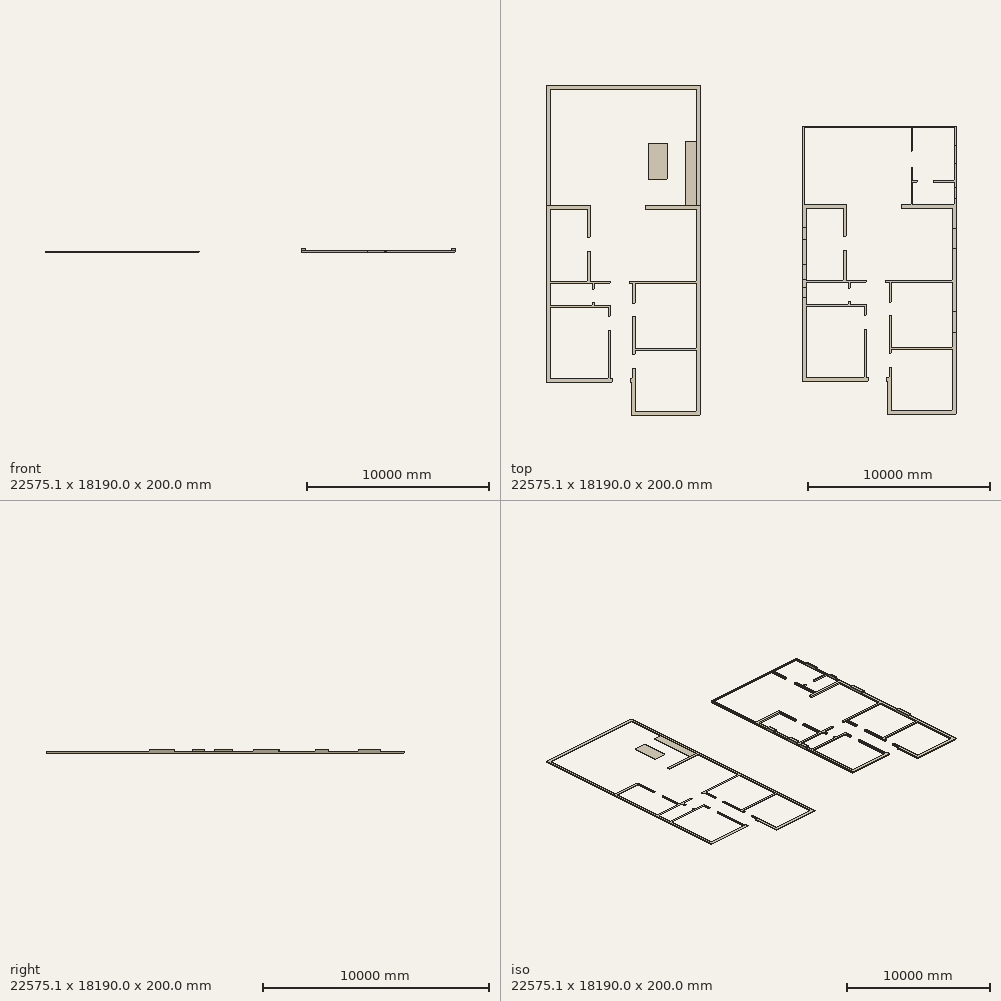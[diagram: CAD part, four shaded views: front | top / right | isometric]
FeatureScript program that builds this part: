
annotation { "Feature Type Name" : "Feature", "Feature Type Description" : "" }
export const myFeature = defineFeature(function(context is Context, id is Id, definition is map)
    precondition{}
    {
        {
            var Q0;
            Q0=qCreatedBy(makeId("Top.planeOp"),FACE);
            var sketch = newSketch(context, id + "F0", { "sketchPlane" : qUnion([Q0])});
            skLineSegment(sketch, "E0", {"start": v(-3410, -4400) * mm, "end": v(-3410, 5380) * mm});
            skLineSegment(sketch, "E1", {"start": v(-3410, 5380) * mm, "end": v(-1010, 5380) * mm});
            skLineSegment(sketch, "E2", {"start": v(5060, 5380) * mm, "end": v(5060, -6200) * mm});
            skLineSegment(sketch, "E3", {"start": v(5060, -6200) * mm, "end": v(1250, -6200) * mm});
            skLineSegment(sketch, "E4", {"start": v(1250, -6200) * mm, "end": v(1250, -4400) * mm});
            skLineSegment(sketch, "E5", {"start": v(240, -4400) * mm, "end": v(-3410, -4400) * mm});
            skLineSegment(sketch, "E6.bottom", {"start": v(1480, -5970) * mm, "end": v(4830, -5970) * mm});
            skLineSegment(sketch, "E6.left", {"start": v(1480, -5970) * mm, "end": v(1480, -3590) * mm});
            skLineSegment(sketch, "E6.right", {"start": v(4830, -5970) * mm, "end": v(4830, -2630) * mm});
            skLineSegment(sketch, "E7", {"start": v(1350, -2840) * mm, "end": v(1350, -730) * mm});
            skLineSegment(sketch, "E8", {"start": v(1350, -730) * mm, "end": v(1480, -730) * mm});
            skLineSegment(sketch, "E9", {"start": v(1480, -730) * mm, "end": v(1480, -2500) * mm});
            skLineSegment(sketch, "E10", {"start": v(1480, -2500) * mm, "end": v(4830, -2500) * mm});
            skLineSegment(sketch, "E11", {"start": v(4830, -2500) * mm, "end": v(4830, 1060) * mm});
            skLineSegment(sketch, "E12", {"start": v(4830, 1060) * mm, "end": v(1480, 1060) * mm});
            skLineSegment(sketch, "E13", {"start": v(1480, 0) * mm, "end": v(1350, 0) * mm});
            skLineSegment(sketch, "E14.bottom", {"start": v(-3180, -4170) * mm, "end": v(0, -4170) * mm});
            skLineSegment(sketch, "E14.top", {"start": v(-3180, -240) * mm, "end": v(0, -240) * mm});
            skLineSegment(sketch, "E14.left", {"start": v(-3180, -4170) * mm, "end": v(-3180, -240) * mm});
            skLineSegment(sketch, "E14.right", {"start": v(0, -4170) * mm, "end": v(0, -1500) * mm});
            skLineSegment(sketch, "E15.bottom", {"start": v(-3180, 1060) * mm, "end": v(-890, 1060) * mm});
            skLineSegment(sketch, "E15.top", {"start": v(-3180, -110) * mm, "end": v(-890, -110) * mm});
            skLineSegment(sketch, "E15.left", {"start": v(-3180, 1060) * mm, "end": v(-3180, -110) * mm});
            skLineSegment(sketch, "E15.right", {"start": v(-890, 1060) * mm, "end": v(-890, 760) * mm});
            skLineSegment(sketch, "E16.bottom", {"start": v(-3180, 5150) * mm, "end": v(-1140, 5150) * mm});
            skLineSegment(sketch, "E16.top", {"start": v(-3180, 1190) * mm, "end": v(-1140, 1190) * mm});
            skLineSegment(sketch, "E16.left", {"start": v(-3180, 5150) * mm, "end": v(-3180, 1190) * mm});
            skLineSegment(sketch, "E16.right", {"start": v(-1140, 5150) * mm, "end": v(-1140, 3600) * mm});
            skLineSegment(sketch, "E17", {"start": v(1350, -2840) * mm, "end": v(1480, -2840) * mm});
            skPoint(sketch, "E18", {"position": v(1480, -3590) * mm});
            skLineSegment(sketch, "E19", {"start": v(1350, -3590) * mm, "end": v(1480, -3590) * mm});
            skPoint(sketch, "E20", {"position": v(0, -750) * mm});
            skPoint(sketch, "E21", {"position": v(0, -1500) * mm});
            skLineSegment(sketch, "E22.trimOffspring", {"start": v(0, -750) * mm, "end": v(0, -240) * mm});
            skLineSegment(sketch, "E23", {"start": v(0, -750) * mm, "end": v(130, -750) * mm});
            skLineSegment(sketch, "E24", {"start": v(130, -750) * mm, "end": v(130, -110) * mm});
            skLineSegment(sketch, "E25", {"start": v(-760, 50) * mm, "end": v(-890, 50) * mm});
            skLineSegment(sketch, "E26", {"start": v(-890, 760) * mm, "end": v(-760, 760) * mm});
            skLineSegment(sketch, "E27.top", {"start": v(-1010, 1190) * mm, "end": v(130, 1190) * mm});
            skLineSegment(sketch, "E28.trimOffspring", {"start": v(-890, 50) * mm, "end": v(-890, -110) * mm});
            skLineSegment(sketch, "E29", {"start": v(-1140, 3600) * mm, "end": v(-1010, 3600) * mm});
            skLineSegment(sketch, "E30", {"start": v(-1010, 2850) * mm, "end": v(-1140, 2850) * mm});
            skLineSegment(sketch, "E31.trimOffspring", {"start": v(-1140, 2850) * mm, "end": v(-1140, 1190) * mm});
            skLineSegment(sketch, "E32.trimOffspring", {"start": v(-1010, 2850) * mm, "end": v(-1010, 1190) * mm});
            skLineSegment(sketch, "E33", {"start": v(-1010, 3600) * mm, "end": v(-1010, 5150) * mm});
            skLineSegment(sketch, "E34", {"start": v(2030, 5150) * mm, "end": v(4830, 5150) * mm});
            skLineSegment(sketch, "E35", {"start": v(4830, 5150) * mm, "end": v(4830, 1190) * mm});
            skLineSegment(sketch, "E36", {"start": v(0, -1500) * mm, "end": v(130, -1500) * mm});
            skLineSegment(sketch, "E37", {"start": v(1350, 1060) * mm, "end": v(1350, 0) * mm});
            skLineSegment(sketch, "E38", {"start": v(1480, 1060) * mm, "end": v(1480, 0) * mm});
            skLineSegment(sketch, "E39", {"start": v(130, -1500) * mm, "end": v(130, -4170) * mm});
            skLineSegment(sketch, "E40", {"start": v(130, -4170) * mm, "end": v(240, -4170) * mm});
            skLineSegment(sketch, "E41", {"start": v(240, -4170) * mm, "end": v(240, -4400) * mm});
            skLineSegment(sketch, "E42", {"start": v(1350, -3590) * mm, "end": v(1350, -4170) * mm});
            skLineSegment(sketch, "E43", {"start": v(1350, -4170) * mm, "end": v(1220, -4170) * mm});
            skLineSegment(sketch, "E44", {"start": v(1220, -4170) * mm, "end": v(1220, -4400) * mm});
            skLineSegment(sketch, "E45", {"start": v(1220, -4400) * mm, "end": v(1250, -4400) * mm});
            skLineSegment(sketch, "E46.bottom", {"start": v(130, 1060) * mm, "end": v(-760, 1060) * mm});
            skLineSegment(sketch, "E46.top", {"start": v(130, -110) * mm, "end": v(-760, -110) * mm});
            skLineSegment(sketch, "E46.right", {"start": v(-760, 1060) * mm, "end": v(-760, 760) * mm});
            skLineSegment(sketch, "E47.trimOffspring", {"start": v(-760, 50) * mm, "end": v(-760, -110) * mm});
            skLineSegment(sketch, "E48", {"start": v(130, 1190) * mm, "end": v(130, 1060) * mm});
            skLineSegment(sketch, "E49", {"start": v(1480, -2840) * mm, "end": v(1480, -2630) * mm});
            skLineSegment(sketch, "E50", {"start": v(1480, -2630) * mm, "end": v(4830, -2630) * mm});
            skLineSegment(sketch, "E51.top", {"start": v(1140, 1060) * mm, "end": v(1350, 1060) * mm});
            skLineSegment(sketch, "E51.left", {"start": v(1140, 1190) * mm, "end": v(1140, 1060) * mm});
            skLineSegment(sketch, "E52", {"start": v(1140, 1190) * mm, "end": v(4830, 1190) * mm});
            skLineSegment(sketch, "E53", {"start": v(-1010, 5150) * mm, "end": v(-1010, 5380) * mm});
            skLineSegment(sketch, "E54", {"start": v(2030, 5150) * mm, "end": v(2030, 5380) * mm});
            skLineSegment(sketch, "E55.trimOffspring", {"start": v(2030, 5380) * mm, "end": v(5060, 5380) * mm});
            skSolve(sketch);
        }
        {
            var Q0;
            Q0=makeQuery(id+"F0.imprint","IMPRINT",FACE,{"disambiguationData":[TD([[makeQuery(id+"F0.imprint","IMPRINT",EDGE,{"derivedFrom":sQuery(id+"F0.wireOp",EDGE,"E0")}),-1.0]])]});
            var sketch = newSketch(context, id + "F1", { "sketchPlane" : qUnion([Q0])});
            skLineSegment(sketch, "E56.0", {"start": v(-3410, 5380) * mm, "end": v(-3180, 5380) * mm});
            skLineSegment(sketch, "E56.1", {"start": v(4830, 5380) * mm, "end": v(5060, 5380) * mm});
            skLineSegment(sketch, "E57.top", {"start": v(-3410, 11990) * mm, "end": v(5060, 11990) * mm});
            skLineSegment(sketch, "E57.left", {"start": v(-3410, 5380) * mm, "end": v(-3410, 11990) * mm});
            skLineSegment(sketch, "E57.right", {"start": v(5060, 5380) * mm, "end": v(5060, 11990) * mm});
            skLineSegment(sketch, "E58.top", {"start": v(-3180, 11760) * mm, "end": v(4830, 11760) * mm});
            skLineSegment(sketch, "E58.left", {"start": v(-3180, 5380) * mm, "end": v(-3180, 11760) * mm});
            skLineSegment(sketch, "E58.right", {"start": v(4830, 5380) * mm, "end": v(4830, 11760) * mm});
            skLineSegment(sketch, "E59.bottom", {"start": v(4830, 5380) * mm, "end": v(4230, 5380) * mm});
            skLineSegment(sketch, "E59.top", {"start": v(4830, 8880) * mm, "end": v(4230, 8880) * mm});
            skLineSegment(sketch, "E59.left", {"start": v(4830, 5380) * mm, "end": v(4830, 8880) * mm});
            skLineSegment(sketch, "E59.right", {"start": v(4230, 5380) * mm, "end": v(4230, 8880) * mm});
            skLineSegment(sketch, "E60.bottom", {"start": v(2230, 6811.8) * mm, "end": v(3230, 6811.8) * mm});
            skLineSegment(sketch, "E60.top", {"start": v(2230, 8811.8) * mm, "end": v(3230, 8811.8) * mm});
            skLineSegment(sketch, "E60.left", {"start": v(2230, 6811.8) * mm, "end": v(2230, 8811.8) * mm});
            skLineSegment(sketch, "E60.right", {"start": v(3230, 6811.8) * mm, "end": v(3230, 8811.8) * mm});
            skSolve(sketch);
        }
        {
            var Q0;
            Q0=makeQuery(id+"F0.imprint","IMPRINT",FACE,{"disambiguationData":[TD([[makeQuery(id+"F0.imprint","IMPRINT",EDGE,{"derivedFrom":sQuery(id+"F0.wireOp",EDGE,"E0")}),-1.0]])]});
            var Q1;
            Q1=makeQuery(id+"F1.imprint","IMPRINT",FACE,{"disambiguationData":[TD([[makeQuery(id+"F1.imprint","IMPRINT",EDGE,{"derivedFrom":sQuery(id+"F1.wireOp",EDGE,"E56.0")}),1.0]])]});
            var Q2;
            Q2=makeQuery(id+"F0.imprint","IMPRINT",FACE,{"disambiguationData":[TD([[makeQuery(id+"F0.imprint","IMPRINT",EDGE,{"derivedFrom":sQuery(id+"F0.wireOp",EDGE,"E2")}),-1.0]])]});
            extrude(context, id + "F2", {"entities" : qUnion([Q0, Q1, Q2]), "depth" : 25 * mm});
        }
        {
            var Q0;
            Q0=makeQuery(id+"F1.imprint","IMPRINT",FACE,{"disambiguationData":[TD([[makeQuery(id+"F1.imprint","IMPRINT",EDGE,{"derivedFrom":sQuery(id+"F1.wireOp",EDGE,"E60.bottom")}),1.0]])]});
            var Q1;
            Q1=makeQuery(id+"F1.imprint","IMPRINT",FACE,{"disambiguationData":[TD([[makeQuery(id+"F1.imprint","IMPRINT",EDGE,{"derivedFrom":sQuery(id+"F1.wireOp",EDGE,"E59.bottom")}),-1.0]])]});
            extrude(context, id + "F3", {"entities" : qUnion([Q0, Q1]), "depth" : 25 * mm});
        }
        {
            var Q0;
            Q0=qCreatedBy(makeId("Top.planeOp"),FACE);
            var sketch = newSketch(context, id + "F4", { "sketchPlane" : qUnion([Q0])});
            skLineSegment(sketch, "E61", {"start": v(10695.13, -4341.89) * mm, "end": v(10695.13, 5438.11) * mm});
            skLineSegment(sketch, "E62", {"start": v(10695.13, 5438.11) * mm, "end": v(13095.13, 5438.11) * mm});
            skLineSegment(sketch, "E63", {"start": v(19165.13, 5438.11) * mm, "end": v(19165.13, -6141.89) * mm});
            skLineSegment(sketch, "E64", {"start": v(19165.13, -6141.89) * mm, "end": v(15355.13, -6141.89) * mm});
            skLineSegment(sketch, "E65", {"start": v(15355.13, -6141.89) * mm, "end": v(15355.13, -4341.89) * mm});
            skLineSegment(sketch, "E66", {"start": v(14345.13, -4341.89) * mm, "end": v(10695.13, -4341.89) * mm});
            skLineSegment(sketch, "E67.bottom", {"start": v(15585.13, -5911.89) * mm, "end": v(18935.13, -5911.89) * mm});
            skLineSegment(sketch, "E67.left", {"start": v(15585.13, -5911.89) * mm, "end": v(15585.13, -3531.89) * mm});
            skLineSegment(sketch, "E67.right", {"start": v(18935.13, -5911.89) * mm, "end": v(18935.13, -2571.89) * mm});
            skLineSegment(sketch, "E68", {"start": v(15455.13, -2781.89) * mm, "end": v(15455.13, -671.89) * mm});
            skLineSegment(sketch, "E69", {"start": v(15455.13, -671.89) * mm, "end": v(15585.13, -671.89) * mm});
            skLineSegment(sketch, "E70", {"start": v(15585.13, -671.89) * mm, "end": v(15585.13, -2441.89) * mm});
            skLineSegment(sketch, "E71", {"start": v(15585.13, -2441.89) * mm, "end": v(18935.13, -2441.89) * mm});
            skLineSegment(sketch, "E72", {"start": v(18935.13, -2441.89) * mm, "end": v(18935.13, 1118.11) * mm});
            skLineSegment(sketch, "E73", {"start": v(18935.13, 1118.11) * mm, "end": v(15585.13, 1118.11) * mm});
            skLineSegment(sketch, "E74", {"start": v(15585.13, 58.11) * mm, "end": v(15455.13, 58.11) * mm});
            skLineSegment(sketch, "E75.bottom", {"start": v(10925.13, -4111.89) * mm, "end": v(14105.13, -4111.89) * mm});
            skLineSegment(sketch, "E75.top", {"start": v(10925.13, -181.89) * mm, "end": v(14105.13, -181.89) * mm});
            skLineSegment(sketch, "E75.left", {"start": v(10925.13, -4111.89) * mm, "end": v(10925.13, -181.89) * mm});
            skLineSegment(sketch, "E75.right", {"start": v(14105.13, -4111.89) * mm, "end": v(14105.13, -1441.89) * mm});
            skLineSegment(sketch, "E76.bottom", {"start": v(10925.13, 1118.11) * mm, "end": v(13215.13, 1118.11) * mm});
            skLineSegment(sketch, "E76.top", {"start": v(10925.13, -51.89) * mm, "end": v(13215.13, -51.89) * mm});
            skLineSegment(sketch, "E76.left", {"start": v(10925.13, 1118.11) * mm, "end": v(10925.13, -51.89) * mm});
            skLineSegment(sketch, "E76.right", {"start": v(13215.13, 1118.11) * mm, "end": v(13215.13, 818.11) * mm});
            skLineSegment(sketch, "E77.bottom", {"start": v(10925.13, 5208.11) * mm, "end": v(12965.13, 5208.11) * mm});
            skLineSegment(sketch, "E77.top", {"start": v(10925.13, 1248.11) * mm, "end": v(12965.13, 1248.11) * mm});
            skLineSegment(sketch, "E77.left", {"start": v(10925.13, 5208.11) * mm, "end": v(10925.13, 1248.11) * mm});
            skLineSegment(sketch, "E77.right", {"start": v(12965.13, 5208.11) * mm, "end": v(12965.13, 3658.11) * mm});
            skLineSegment(sketch, "E78", {"start": v(15455.13, -2781.89) * mm, "end": v(15585.13, -2781.89) * mm});
            skPoint(sketch, "E79", {"position": v(15585.13, -3531.89) * mm});
            skLineSegment(sketch, "E80", {"start": v(15455.13, -3531.89) * mm, "end": v(15585.13, -3531.89) * mm});
            skPoint(sketch, "E81", {"position": v(14105.13, -691.89) * mm});
            skPoint(sketch, "E82", {"position": v(14105.13, -1441.89) * mm});
            skLineSegment(sketch, "E83.trimOffspring", {"start": v(14105.13, -691.89) * mm, "end": v(14105.13, -181.89) * mm});
            skLineSegment(sketch, "E84", {"start": v(14105.13, -691.89) * mm, "end": v(14235.13, -691.89) * mm});
            skLineSegment(sketch, "E85", {"start": v(14235.13, -691.89) * mm, "end": v(14235.13, -51.89) * mm});
            skLineSegment(sketch, "E86", {"start": v(13345.13, 108.11) * mm, "end": v(13215.13, 108.11) * mm});
            skLineSegment(sketch, "E87", {"start": v(13215.13, 818.11) * mm, "end": v(13345.13, 818.11) * mm});
            skLineSegment(sketch, "E88.top", {"start": v(13095.13, 1248.11) * mm, "end": v(14235.13, 1248.11) * mm});
            skLineSegment(sketch, "E89.trimOffspring", {"start": v(13215.13, 108.11) * mm, "end": v(13215.13, -51.89) * mm});
            skLineSegment(sketch, "E90", {"start": v(12965.13, 3658.11) * mm, "end": v(13095.13, 3658.11) * mm});
            skLineSegment(sketch, "E91", {"start": v(13095.13, 2908.11) * mm, "end": v(12965.13, 2908.11) * mm});
            skLineSegment(sketch, "E92.trimOffspring", {"start": v(12965.13, 2908.11) * mm, "end": v(12965.13, 1248.11) * mm});
            skLineSegment(sketch, "E93.trimOffspring", {"start": v(13095.13, 2908.11) * mm, "end": v(13095.13, 1248.11) * mm});
            skLineSegment(sketch, "E94", {"start": v(13095.13, 3658.11) * mm, "end": v(13095.13, 5208.11) * mm});
            skLineSegment(sketch, "E95", {"start": v(16135.13, 5208.11) * mm, "end": v(18935.13, 5208.11) * mm});
            skLineSegment(sketch, "E96", {"start": v(18935.13, 5208.11) * mm, "end": v(18935.13, 1248.11) * mm});
            skLineSegment(sketch, "E97", {"start": v(14105.13, -1441.89) * mm, "end": v(14235.13, -1441.89) * mm});
            skLineSegment(sketch, "E98", {"start": v(15455.13, 1118.11) * mm, "end": v(15455.13, 58.11) * mm});
            skLineSegment(sketch, "E99", {"start": v(15585.13, 1118.11) * mm, "end": v(15585.13, 58.11) * mm});
            skLineSegment(sketch, "E100", {"start": v(14235.13, -1441.89) * mm, "end": v(14235.13, -4111.89) * mm});
            skLineSegment(sketch, "E101", {"start": v(14235.13, -4111.89) * mm, "end": v(14345.13, -4111.89) * mm});
            skLineSegment(sketch, "E102", {"start": v(14345.13, -4111.89) * mm, "end": v(14345.13, -4341.89) * mm});
            skLineSegment(sketch, "E103", {"start": v(15455.13, -3531.89) * mm, "end": v(15455.13, -4111.89) * mm});
            skLineSegment(sketch, "E104", {"start": v(15455.13, -4111.89) * mm, "end": v(15325.13, -4111.89) * mm});
            skLineSegment(sketch, "E105", {"start": v(15325.13, -4111.89) * mm, "end": v(15325.13, -4341.89) * mm});
            skLineSegment(sketch, "E106", {"start": v(15325.13, -4341.89) * mm, "end": v(15355.13, -4341.89) * mm});
            skLineSegment(sketch, "E107.bottom", {"start": v(14235.13, 1118.11) * mm, "end": v(13345.13, 1118.11) * mm});
            skLineSegment(sketch, "E107.top", {"start": v(14235.13, -51.89) * mm, "end": v(13345.13, -51.89) * mm});
            skLineSegment(sketch, "E107.right", {"start": v(13345.13, 1118.11) * mm, "end": v(13345.13, 818.11) * mm});
            skLineSegment(sketch, "E108.trimOffspring", {"start": v(13345.13, 108.11) * mm, "end": v(13345.13, -51.89) * mm});
            skLineSegment(sketch, "E109", {"start": v(14235.13, 1248.11) * mm, "end": v(14235.13, 1118.11) * mm});
            skLineSegment(sketch, "E110", {"start": v(15585.13, -2781.89) * mm, "end": v(15585.13, -2571.89) * mm});
            skLineSegment(sketch, "E111", {"start": v(15585.13, -2571.89) * mm, "end": v(18935.13, -2571.89) * mm});
            skLineSegment(sketch, "E112.top", {"start": v(15245.13, 1118.11) * mm, "end": v(15455.13, 1118.11) * mm});
            skLineSegment(sketch, "E112.left", {"start": v(15245.13, 1248.11) * mm, "end": v(15245.13, 1118.11) * mm});
            skLineSegment(sketch, "E113", {"start": v(15245.13, 1248.11) * mm, "end": v(18935.13, 1248.11) * mm});
            skLineSegment(sketch, "E114", {"start": v(13095.13, 5208.11) * mm, "end": v(13095.13, 5438.11) * mm});
            skLineSegment(sketch, "E115", {"start": v(16135.13, 5208.11) * mm, "end": v(16135.13, 5438.11) * mm});
            skLineSegment(sketch, "E116.trimOffspring", {"start": v(16135.13, 5438.11) * mm, "end": v(19165.13, 5438.11) * mm});
            skLineSegment(sketch, "E117.bottom", {"start": v(18935.13, -461.89) * mm, "end": v(19165.13, -461.89) * mm});
            skLineSegment(sketch, "E117.top", {"start": v(18935.13, -1601.89) * mm, "end": v(19165.13, -1601.89) * mm});
            skLineSegment(sketch, "E117.left", {"start": v(18935.13, -461.89) * mm, "end": v(18935.13, -1601.89) * mm});
            skLineSegment(sketch, "E117.right", {"start": v(19165.13, -461.89) * mm, "end": v(19165.13, -1601.89) * mm});
            skLineSegment(sketch, "E118", {"start": v(10695.13, 5438.11) * mm, "end": v(10695.13, 9748.11) * mm});
            skLineSegment(sketch, "E119", {"start": v(10695.13, 9748.11) * mm, "end": v(19165.13, 9748.11) * mm});
            skLineSegment(sketch, "E120", {"start": v(19165.13, 9748.11) * mm, "end": v(19165.13, 5438.11) * mm});
            skLineSegment(sketch, "E121", {"start": v(19065.13, 5438.11) * mm, "end": v(19065.13, 9648.11) * mm});
            skLineSegment(sketch, "E122", {"start": v(19065.13, 9648.11) * mm, "end": v(10795.13, 9648.11) * mm});
            skLineSegment(sketch, "E123", {"start": v(10795.13, 9648.11) * mm, "end": v(10795.13, 5438.11) * mm});
            skLineSegment(sketch, "E124.bottom", {"start": v(11775.13, 9748.11) * mm, "end": v(13545.13, 9748.11) * mm});
            skLineSegment(sketch, "E124.top", {"start": v(11775.13, 9648.11) * mm, "end": v(13545.13, 9648.11) * mm});
            skLineSegment(sketch, "E124.left", {"start": v(11775.13, 9748.11) * mm, "end": v(11775.13, 9648.11) * mm});
            skLineSegment(sketch, "E124.right", {"start": v(13545.13, 9748.11) * mm, "end": v(13545.13, 9648.11) * mm});
            skLineSegment(sketch, "E125.bottom", {"start": v(14645.13, 9748.11) * mm, "end": v(16425.13, 9748.11) * mm});
            skLineSegment(sketch, "E125.top", {"start": v(14645.13, 9648.11) * mm, "end": v(16425.13, 9648.11) * mm});
            skLineSegment(sketch, "E125.left", {"start": v(14645.13, 9748.11) * mm, "end": v(14645.13, 9648.11) * mm});
            skLineSegment(sketch, "E125.right", {"start": v(16425.13, 9748.11) * mm, "end": v(16425.13, 9648.11) * mm});
            skLineSegment(sketch, "E126.bottom", {"start": v(11945.13, -4111.89) * mm, "end": v(13105.13, -4111.89) * mm});
            skLineSegment(sketch, "E126.top", {"start": v(11945.13, -4341.89) * mm, "end": v(13105.13, -4341.89) * mm});
            skLineSegment(sketch, "E126.left", {"start": v(11945.13, -4111.89) * mm, "end": v(11945.13, -4341.89) * mm});
            skLineSegment(sketch, "E126.right", {"start": v(13105.13, -4111.89) * mm, "end": v(13105.13, -4341.89) * mm});
            skLineSegment(sketch, "E127.bottom", {"start": v(16485.13, -5911.89) * mm, "end": v(18025.13, -5911.89) * mm});
            skLineSegment(sketch, "E127.top", {"start": v(16485.13, -6141.89) * mm, "end": v(18025.13, -6141.89) * mm});
            skLineSegment(sketch, "E127.left", {"start": v(16485.13, -5911.89) * mm, "end": v(16485.13, -6141.89) * mm});
            skLineSegment(sketch, "E127.right", {"start": v(18025.13, -5911.89) * mm, "end": v(18025.13, -6141.89) * mm});
            skLineSegment(sketch, "E128.bottom", {"start": v(10695.13, 4178.11) * mm, "end": v(10925.13, 4178.11) * mm});
            skLineSegment(sketch, "E128.top", {"start": v(10695.13, 3528.11) * mm, "end": v(10925.13, 3528.11) * mm});
            skLineSegment(sketch, "E128.left", {"start": v(10695.13, 4178.11) * mm, "end": v(10695.13, 3528.11) * mm});
            skLineSegment(sketch, "E128.right", {"start": v(10925.13, 4178.11) * mm, "end": v(10925.13, 3528.11) * mm});
            skLineSegment(sketch, "E129.bottom", {"start": v(10695.13, 2098.11) * mm, "end": v(10925.13, 2098.11) * mm});
            skLineSegment(sketch, "E129.top", {"start": v(10695.13, 1298.11) * mm, "end": v(10925.13, 1298.11) * mm});
            skLineSegment(sketch, "E129.left", {"start": v(10695.13, 2098.11) * mm, "end": v(10695.13, 1298.11) * mm});
            skLineSegment(sketch, "E129.right", {"start": v(10925.13, 2098.11) * mm, "end": v(10925.13, 1298.11) * mm});
            skLineSegment(sketch, "E130.bottom", {"start": v(16665.13, 5438.11) * mm, "end": v(16765.13, 5438.11) * mm});
            skLineSegment(sketch, "E130.top", {"start": v(16665.13, 9648.11) * mm, "end": v(16765.13, 9648.11) * mm});
            skLineSegment(sketch, "E130.left", {"start": v(16665.13, 5438.11) * mm, "end": v(16665.13, 7443.63) * mm});
            skLineSegment(sketch, "E130.right", {"start": v(16765.13, 5438.11) * mm, "end": v(16765.13, 7443.63) * mm});
            skLineSegment(sketch, "E131.bottom", {"start": v(19065.13, 6648.11) * mm, "end": v(17888.2, 6648.11) * mm});
            skLineSegment(sketch, "E131.top", {"start": v(19065.13, 6748.11) * mm, "end": v(17888.2, 6748.11) * mm});
            skLineSegment(sketch, "E131.left", {"start": v(19065.13, 6648.11) * mm, "end": v(19065.13, 6748.11) * mm});
            skLineSegment(sketch, "E131.right", {"start": v(16765.13, 6648.11) * mm, "end": v(16765.13, 6748.11) * mm});
            skLineSegment(sketch, "E132.bottom", {"start": v(16765.13, 7443.63) * mm, "end": v(16665.13, 7443.63) * mm});
            skLineSegment(sketch, "E132.top", {"start": v(16765.13, 8322.22) * mm, "end": v(16665.13, 8322.22) * mm});
            skLineSegment(sketch, "E133.trimOffspring", {"start": v(16765.13, 8322.22) * mm, "end": v(16765.13, 9648.11) * mm});
            skLineSegment(sketch, "E134.trimOffspring", {"start": v(16665.13, 8322.22) * mm, "end": v(16665.13, 9648.11) * mm});
            skLineSegment(sketch, "E135.left", {"start": v(17035, 6748.11) * mm, "end": v(17035, 6648.11) * mm});
            skLineSegment(sketch, "E135.right", {"start": v(17888.2, 6748.11) * mm, "end": v(17888.2, 6648.11) * mm});
            skLineSegment(sketch, "E136.trimOffspring", {"start": v(17035, 6748.11) * mm, "end": v(16765.13, 6748.11) * mm});
            skLineSegment(sketch, "E137.trimOffspring", {"start": v(17035, 6648.11) * mm, "end": v(16765.13, 6648.11) * mm});
            skLineSegment(sketch, "E138.bottom", {"start": v(19065.13, 8678.11) * mm, "end": v(19165.13, 8678.11) * mm});
            skLineSegment(sketch, "E138.top", {"start": v(19065.13, 7708.11) * mm, "end": v(19165.13, 7708.11) * mm});
            skLineSegment(sketch, "E138.left", {"start": v(19065.13, 8678.11) * mm, "end": v(19065.13, 7708.11) * mm});
            skLineSegment(sketch, "E138.right", {"start": v(19165.13, 8678.11) * mm, "end": v(19165.13, 7708.11) * mm});
            skLineSegment(sketch, "E139.bottom", {"start": v(19065.13, 6358.11) * mm, "end": v(19165.13, 6358.11) * mm});
            skLineSegment(sketch, "E139.top", {"start": v(19065.13, 5758.11) * mm, "end": v(19165.13, 5758.11) * mm});
            skLineSegment(sketch, "E139.left", {"start": v(19065.13, 6358.11) * mm, "end": v(19065.13, 5758.11) * mm});
            skLineSegment(sketch, "E139.right", {"start": v(19165.13, 6358.11) * mm, "end": v(19165.13, 5758.11) * mm});
            skLineSegment(sketch, "E140.bottom", {"start": v(10695.13, 838.11) * mm, "end": v(10925.13, 838.11) * mm});
            skLineSegment(sketch, "E140.top", {"start": v(10695.13, 318.11) * mm, "end": v(10925.13, 318.11) * mm});
            skLineSegment(sketch, "E140.left", {"start": v(10695.13, 838.11) * mm, "end": v(10695.13, 318.11) * mm});
            skLineSegment(sketch, "E140.right", {"start": v(10925.13, 838.11) * mm, "end": v(10925.13, 318.11) * mm});
            skLineSegment(sketch, "E141.bottom", {"start": v(18935.13, 4118.11) * mm, "end": v(19165.13, 4118.11) * mm});
            skLineSegment(sketch, "E141.top", {"start": v(18935.13, 3018.11) * mm, "end": v(19165.13, 3018.11) * mm});
            skLineSegment(sketch, "E141.left", {"start": v(18935.13, 4118.11) * mm, "end": v(18935.13, 3018.11) * mm});
            skLineSegment(sketch, "E141.right", {"start": v(19165.13, 4118.11) * mm, "end": v(19165.13, 3018.11) * mm});
            skSolve(sketch);
        }
        {
            var Q0;
            Q0 = qSketchRegion(id + "F4", true);
            extrude(context, id + "F5", {"entities" : qUnion([Q0]), "depth" : 100 * mm});
        }
        {
            var Q0;
            Q0=makeQuery(id+"F4.imprint","IMPRINT",FACE,{"disambiguationData":[TD([[makeQuery(id+"F4.imprint","IMPRINT",EDGE,{"derivedFrom":sQuery(id+"F4.wireOp",EDGE,"E124.bottom")}),-1.0]])]});
            var Q1;
            Q1=makeQuery(id+"F4.imprint","IMPRINT",FACE,{"disambiguationData":[TD([[makeQuery(id+"F4.imprint","IMPRINT",EDGE,{"derivedFrom":sQuery(id+"F4.wireOp",EDGE,"E125.bottom")}),-1.0]])]});
            var Q2;
            Q2=makeQuery(id+"F4.imprint","IMPRINT",FACE,{"disambiguationData":[TD([[makeQuery(id+"F4.imprint","IMPRINT",EDGE,{"derivedFrom":sQuery(id+"F4.wireOp",EDGE,"E138.bottom")}),-1.0]])]});
            var Q3;
            Q3=makeQuery(id+"F4.imprint","IMPRINT",FACE,{"disambiguationData":[TD([[makeQuery(id+"F4.imprint","IMPRINT",EDGE,{"derivedFrom":sQuery(id+"F4.wireOp",EDGE,"E139.bottom")}),-1.0]])]});
            var Q4;
            Q4=makeQuery(id+"F4.imprint","IMPRINT",FACE,{"disambiguationData":[TD([[makeQuery(id+"F4.imprint","IMPRINT",EDGE,{"derivedFrom":sQuery(id+"F4.wireOp",EDGE,"E141.bottom")}),-1.0]])]});
            var Q5;
            Q5=makeQuery(id+"F4.imprint","IMPRINT",FACE,{"disambiguationData":[TD([[makeQuery(id+"F4.imprint","IMPRINT",EDGE,{"derivedFrom":sQuery(id+"F4.wireOp",EDGE,"E117.bottom")}),-1.0]])]});
            var Q6;
            Q6=makeQuery(id+"F4.imprint","IMPRINT",FACE,{"disambiguationData":[TD([[makeQuery(id+"F4.imprint","IMPRINT",EDGE,{"derivedFrom":sQuery(id+"F4.wireOp",EDGE,"E127.bottom")}),-1.0]])]});
            var Q7;
            Q7=makeQuery(id+"F4.imprint","IMPRINT",FACE,{"disambiguationData":[TD([[makeQuery(id+"F4.imprint","IMPRINT",EDGE,{"derivedFrom":sQuery(id+"F4.wireOp",EDGE,"E126.bottom")}),-1.0]])]});
            var Q8;
            Q8=makeQuery(id+"F4.imprint","IMPRINT",FACE,{"disambiguationData":[TD([[makeQuery(id+"F4.imprint","IMPRINT",EDGE,{"derivedFrom":sQuery(id+"F4.wireOp",EDGE,"E140.bottom")}),-1.0]])]});
            var Q9;
            Q9=makeQuery(id+"F4.imprint","IMPRINT",FACE,{"disambiguationData":[TD([[makeQuery(id+"F4.imprint","IMPRINT",EDGE,{"derivedFrom":sQuery(id+"F4.wireOp",EDGE,"E129.bottom")}),-1.0]])]});
            var Q10;
            Q10=makeQuery(id+"F4.imprint","IMPRINT",FACE,{"disambiguationData":[TD([[makeQuery(id+"F4.imprint","IMPRINT",EDGE,{"derivedFrom":sQuery(id+"F4.wireOp",EDGE,"E128.bottom")}),-1.0]])]});
            extrude(context, id + "F6", {"entities" : qUnion([Q0, Q1, Q2, Q3, Q4, Q5, Q6, Q7, Q8, Q9, Q10]), "operationType" : NewBodyOperationType.ADD, "depth" : 200 * mm});
        }
    });
